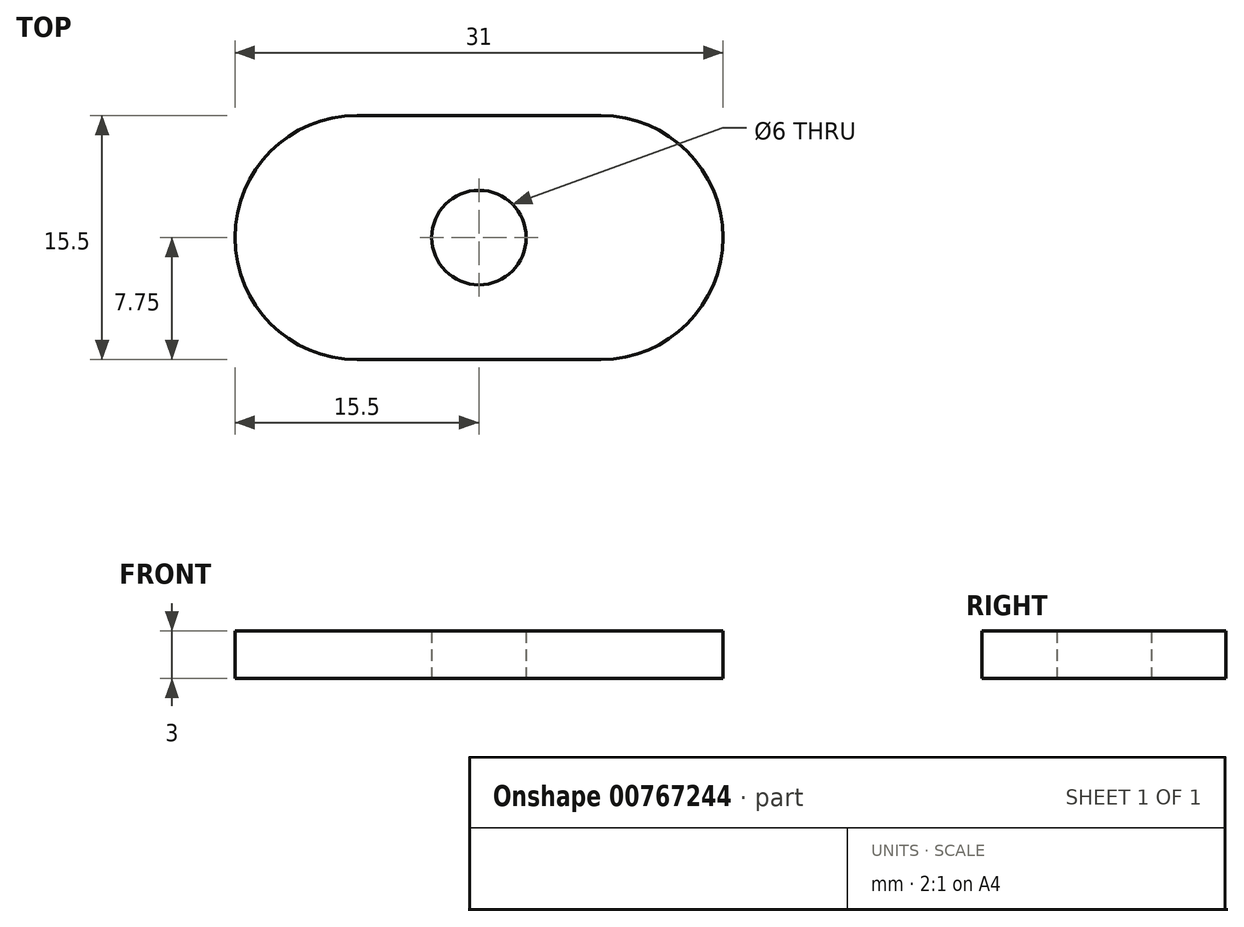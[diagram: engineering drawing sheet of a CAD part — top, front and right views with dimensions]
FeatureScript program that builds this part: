
annotation { "Feature Type Name" : "Feature", "Feature Type Description" : "" }
export const myFeature = defineFeature(function(context is Context, id is Id, definition is map)
    precondition{}
    {
        {
            var Q0;
            Q0=qCreatedBy(makeId("Top.planeOp"),FACE);
            var sketch = newSketch(context, id + "F0", { "sketchPlane" : qUnion([Q0])});
            skLineSegment(sketch, "E0.bottom", {"start": v(7.75, 7.75) * mm, "end": v(-7.75, 7.75) * mm});
            skLineSegment(sketch, "E0.top", {"start": v(7.75, -7.75) * mm, "end": v(-7.75, -7.75) * mm});
            skLineSegment(sketch, "E0.left", {"start": v(7.75, 7.75) * mm, "end": v(7.75, -7.75) * mm});
            skLineSegment(sketch, "E0.right", {"start": v(-7.75, 7.75) * mm, "end": v(-7.75, -7.75) * mm});
            skPoint(sketch, "E0.middle", {"position": v(0, 0) * mm});
            skArc(sketch, "E1", {"start": v(-7.75, -7.75) * mm, "mid": v(-15.5, 0) * mm, "end": v(-7.75, 7.75) * mm});
            skArc(sketch, "E2", {"start": v(7.75, -7.75) * mm, "mid": v(15.5, 0) * mm, "end": v(7.75, 7.75) * mm});
            skCircle(sketch, "E3", {"center": v(0, 0) * mm, "radius": 3 * mm});
            skSolve(sketch);
        }
        {
            var Q0;
            Q0 = qSketchRegion(id + "F0", true);
            extrude(context, id + "F1", {"entities" : qUnion([Q0]), "depth" : 3 * mm, "offsetDistance" : 25 * mm});
        }
    });
